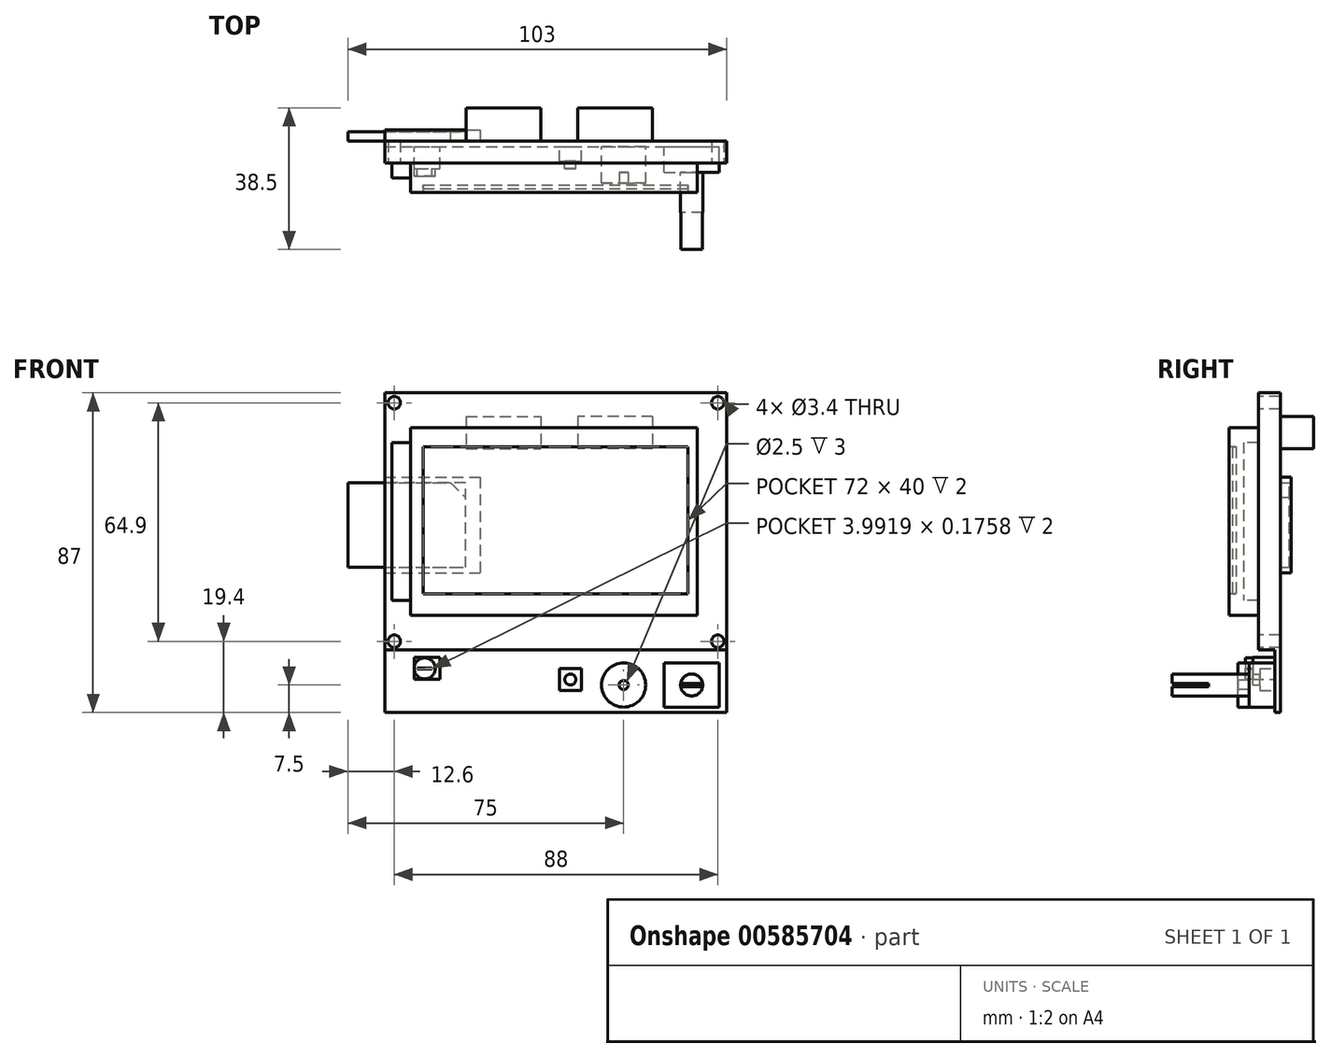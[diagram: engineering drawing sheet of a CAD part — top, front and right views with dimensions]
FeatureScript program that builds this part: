
annotation { "Feature Type Name" : "Feature", "Feature Type Description" : "" }
export const myFeature = defineFeature(function(context is Context, id is Id, definition is map)
    precondition{}
    {
        {
            var Q0;
            Q0=qCreatedBy(makeId("Front.planeOp"),FACE);
            var sketch = newSketch(context, id + "F0", { "sketchPlane" : qUnion([Q0])});
            skLineSegment(sketch, "E0.bottom", {"start": v(0, 0) * mm, "end": v(93, 0) * mm});
            skLineSegment(sketch, "E0.top", {"start": v(0, -87) * mm, "end": v(93, -87) * mm});
            skLineSegment(sketch, "E0.left", {"start": v(0, 0) * mm, "end": v(0, -87) * mm});
            skLineSegment(sketch, "E0.right", {"start": v(93, 0) * mm, "end": v(93, -87) * mm});
            skSolve(sketch);
        }
        {
            var Q0;
            Q0 = qSketchRegion(id + "F0", true);
            extrude(context, id + "F1", {"entities" : qUnion([Q0]), "oppositeDirection" : true, "depth" : 6 * mm, "offsetDistance" : 25 * mm});
        }
        {
            var Q0;
            Q0=makeQuery(id+"F1.opExtrude","CAP_FACE",FACE,{"disambiguationData":[OSD([sQuery(id+"F0.wireOp",EDGE,"E0.bottom"),sQuery(id+"F0.wireOp",EDGE,"E0.top"),sQuery(id+"F0.wireOp",EDGE,"E0.left"),sQuery(id+"F0.wireOp",EDGE,"E0.right")])],"isStart":true});
            var sketch = newSketch(context, id + "F2", { "sketchPlane" : qUnion([Q0])});
            skLineSegment(sketch, "E1.bottom", {"start": v(7, -9.5) * mm, "end": v(85, -9.5) * mm});
            skLineSegment(sketch, "E1.top", {"start": v(7, -60.5) * mm, "end": v(85, -60.5) * mm});
            skLineSegment(sketch, "E1.left", {"start": v(7, -9.5) * mm, "end": v(7, -60.5) * mm});
            skLineSegment(sketch, "E1.right", {"start": v(85, -9.5) * mm, "end": v(85, -60.5) * mm});
            skSolve(sketch);
        }
        {
            var Q0;
            Q0 = qSketchRegion(id + "F2", true);
            extrude(context, id + "F3", {"entities" : qUnion([Q0]), "operationType" : NewBodyOperationType.ADD, "depth" : 8 * mm, "offsetDistance" : 25 * mm});
        }
        {
            var Q0;
            Q0=makeQuery(id+"F3.opExtrude","CAP_FACE",FACE,{"disambiguationData":[OSD([sQuery(id+"F2.wireOp",EDGE,"E1.bottom"),sQuery(id+"F2.wireOp",EDGE,"E1.top"),sQuery(id+"F2.wireOp",EDGE,"E1.left"),sQuery(id+"F2.wireOp",EDGE,"E1.right")])],"isStart":false});
            var sketch = newSketch(context, id + "F4", { "sketchPlane" : qUnion([Q0])});
            skLineSegment(sketch, "E2.bottom", {"start": v(10.5, -14.75) * mm, "end": v(82.5, -14.75) * mm});
            skLineSegment(sketch, "E2.top", {"start": v(10.5, -54.75) * mm, "end": v(82.5, -54.75) * mm});
            skLineSegment(sketch, "E2.left", {"start": v(10.5, -14.75) * mm, "end": v(10.5, -54.75) * mm});
            skLineSegment(sketch, "E2.right", {"start": v(82.5, -14.75) * mm, "end": v(82.5, -54.75) * mm});
            skSolve(sketch);
        }
        {
            var Q0;
            Q0 = qSketchRegion(id + "F4", true);
            extrude(context, id + "F5", {"entities" : qUnion([Q0]), "operationType" : NewBodyOperationType.REMOVE, "oppositeDirection" : true, "depth" : 2 * mm, "offsetDistance" : 25 * mm});
        }
        {
            var Q0;
            Q0=makeQuery(id+"F1.opExtrude","CAP_FACE",FACE,{"disambiguationData":[OSD([sQuery(id+"F0.wireOp",EDGE,"E0.bottom"),sQuery(id+"F0.wireOp",EDGE,"E0.top"),sQuery(id+"F0.wireOp",EDGE,"E0.left"),sQuery(id+"F0.wireOp",EDGE,"E0.right")])],"isStart":true});
            var sketch = newSketch(context, id + "F6", { "sketchPlane" : qUnion([Q0])});
            skCircle(sketch, "E3", {"center": v(2.6, -2.7) * mm, "radius": 1.7 * mm});
            skCircle(sketch, "E4.MirrorC", {"center": v(90.6, -2.7) * mm, "radius": 1.7 * mm});
            skLineSegment(sketch, "E5", {"start": v(0, -70) * mm, "end": v(93, -70) * mm, "construction": true});
            skCircle(sketch, "E6.MirrorC", {"center": v(90.6, -67.6) * mm, "radius": 1.7 * mm});
            skCircle(sketch, "E7.MirrorC", {"center": v(2.6, -67.6) * mm, "radius": 1.7 * mm});
            skPoint(sketch, "E8.0", {"position": v(93, 0) * mm});
            skLineSegment(sketch, "E9.0", {"start": v(0, 0) * mm, "end": v(93, 0) * mm, "construction": true});
            skLineSegment(sketch, "E10.0", {"start": v(93, 0) * mm, "end": v(93, -87) * mm, "construction": true});
            skSolve(sketch);
        }
        {
            var Q0;
            Q0 = qSketchRegion(id + "F6", true);
            extrude(context, id + "F7", {"entities" : qUnion([Q0]), "operationType" : NewBodyOperationType.REMOVE, "oppositeDirection" : true, "depth" : 25 * mm, "offsetDistance" : 25 * mm});
        }
        {
            var Q0;
            Q0=makeQuery(id+"F3.opExtrude","SWEPT_FACE",FACE,{"disambiguationData":[OSD([sQuery(id+"F2.wireOp",EDGE,"E1.left")])]});
            var sketch = newSketch(context, id + "F8", { "sketchPlane" : qUnion([Q0])});
            skLineSegment(sketch, "E11.bottom", {"start": v(0, -13.5) * mm, "end": v(4, -13.5) * mm});
            skLineSegment(sketch, "E11.top", {"start": v(0, -56.5) * mm, "end": v(4, -56.5) * mm});
            skLineSegment(sketch, "E11.left", {"start": v(0, -13.5) * mm, "end": v(0, -56.5) * mm});
            skLineSegment(sketch, "E11.right", {"start": v(4, -13.5) * mm, "end": v(4, -56.5) * mm});
            skSolve(sketch);
        }
        {
            var Q0;
            Q0 = qSketchRegion(id + "F8", true);
            extrude(context, id + "F9", {"entities" : qUnion([Q0]), "operationType" : NewBodyOperationType.ADD, "depth" : 5 * mm, "offsetDistance" : 25 * mm});
        }
        {
            var Q0;
            Q0=makeQuery(id+"F6.imprint","IMPRINT",FACE,{"disambiguationData":[TD([[makeQuery(id+"F6.imprint","IMPRINT",EDGE,{"derivedFrom":sQuery(id+"F6.wireOp",EDGE,"E3")}),-1.0]])]});
            var sketch = newSketch(context, id + "F10", { "sketchPlane" : qUnion([Q0])});
            skLineSegment(sketch, "E12.0", {"start": v(0, -70) * mm, "end": v(93, -70) * mm});
            skLineSegment(sketch, "E13.0", {"start": v(0, -70) * mm, "end": v(0, -87) * mm});
            skLineSegment(sketch, "E14.0", {"start": v(0, -87) * mm, "end": v(93, -87) * mm});
            skLineSegment(sketch, "E15.0", {"start": v(93, -70) * mm, "end": v(93, -87) * mm});
            skPoint(sketch, "E16.orphan", {"position": v(0, 0) * mm});
            skPoint(sketch, "E17.orphan", {"position": v(93, 0) * mm});
            skSolve(sketch);
        }
        {
            var Q0;
            Q0 = qSketchRegion(id + "F10", true);
            extrude(context, id + "F11", {"entities" : qUnion([Q0]), "operationType" : NewBodyOperationType.REMOVE, "oppositeDirection" : true, "depth" : 4.5 * mm, "offsetDistance" : 25 * mm});
        }
        {
            var Q0;
            Q0=makeQuery(id+"F11.boolean.opBoolean","COPY",FACE,{"derivedFrom":makeQuery(id+"F11.opExtrude","CAP_FACE",FACE,{"disambiguationData":[OSD([sQuery(id+"F10.wireOp",EDGE,"E12.0"),sQuery(id+"F10.wireOp",EDGE,"E13.0"),sQuery(id+"F10.wireOp",EDGE,"E14.0"),sQuery(id+"F10.wireOp",EDGE,"E15.0")])],"isStart":false})});
            var sketch = newSketch(context, id + "F12", { "sketchPlane" : qUnion([Q0])});
            skLineSegment(sketch, "E18.bottom", {"start": v(76, -73.5) * mm, "end": v(91, -73.5) * mm});
            skLineSegment(sketch, "E18.top", {"start": v(76, -85.5) * mm, "end": v(91, -85.5) * mm});
            skLineSegment(sketch, "E18.left", {"start": v(76, -73.5) * mm, "end": v(76, -85.5) * mm});
            skLineSegment(sketch, "E18.right", {"start": v(91, -73.5) * mm, "end": v(91, -85.5) * mm});
            skLineSegment(sketch, "E19.bottom", {"start": v(47.5, -75) * mm, "end": v(53.5, -75) * mm});
            skLineSegment(sketch, "E19.top", {"start": v(47.5, -81) * mm, "end": v(53.5, -81) * mm});
            skLineSegment(sketch, "E19.left", {"start": v(47.5, -75) * mm, "end": v(47.5, -81) * mm});
            skLineSegment(sketch, "E19.right", {"start": v(53.5, -75) * mm, "end": v(53.5, -81) * mm});
            skLineSegment(sketch, "E20.bottom", {"start": v(8, -72) * mm, "end": v(15, -72) * mm});
            skLineSegment(sketch, "E20.top", {"start": v(8, -78) * mm, "end": v(15, -78) * mm});
            skLineSegment(sketch, "E20.left", {"start": v(8, -72) * mm, "end": v(8, -78) * mm});
            skLineSegment(sketch, "E20.right", {"start": v(15, -72) * mm, "end": v(15, -78) * mm});
            skCircle(sketch, "E21", {"center": v(65, -79.5) * mm, "radius": 6 * mm});
            skLineSegment(sketch, "E22", {"start": v(53.5, -78) * mm, "end": v(47.5, -78) * mm, "construction": true});
            skSolve(sketch);
        }
        {
            var Q0;
            Q0 = qSketchRegion(id + "F12", true);
            extrude(context, id + "F13", {"entities" : qUnion([Q0]), "operationType" : NewBodyOperationType.ADD, "depth" : 4 * mm, "offsetDistance" : 25 * mm});
        }
        {
            var Q0;
            Q0=makeQuery(id+"F13.opExtrude","CAP_FACE",FACE,{"disambiguationData":[OSD([sQuery(id+"F12.wireOp",EDGE,"E18.bottom"),sQuery(id+"F12.wireOp",EDGE,"E18.top"),sQuery(id+"F12.wireOp",EDGE,"E18.left"),sQuery(id+"F12.wireOp",EDGE,"E18.right")])],"isStart":false});
            extrude(context, id + "F14", {"entities" : qUnion([Q0]), "operationType" : NewBodyOperationType.ADD, "depth" : 3 * mm, "offsetDistance" : 25 * mm});
        }
        {
            var Q0;
            Q0=makeQuery(id+"F13.opExtrude","CAP_FACE",FACE,{"disambiguationData":[OSD([sQuery(id+"F12.wireOp",EDGE,"E20.bottom"),sQuery(id+"F12.wireOp",EDGE,"E20.top"),sQuery(id+"F12.wireOp",EDGE,"E20.left"),sQuery(id+"F12.wireOp",EDGE,"E20.right")])],"isStart":false});
            extrude(context, id + "F15", {"entities" : qUnion([Q0]), "operationType" : NewBodyOperationType.ADD, "depth" : 2 * mm, "offsetDistance" : 25 * mm});
        }
        {
            var Q0;
            Q0=makeQuery(id+"F13.opExtrude","CAP_FACE",FACE,{"disambiguationData":[OSD([sQuery(id+"F12.wireOp",EDGE,"E21")])],"isStart":false});
            extrude(context, id + "F16", {"entities" : qUnion([Q0]), "operationType" : NewBodyOperationType.ADD, "depth" : 6 * mm, "offsetDistance" : 25 * mm});
        }
        {
            var Q0;
            Q0=makeQuery(id+"F15.opExtrude","CAP_FACE",FACE,{"disambiguationData":[OSD([sQuery(id+"F12.wireOp",EDGE,"E20.bottom"),sQuery(id+"F12.wireOp",EDGE,"E20.top"),sQuery(id+"F12.wireOp",EDGE,"E20.left"),sQuery(id+"F12.wireOp",EDGE,"E20.right")])],"isStart":false});
            var sketch = newSketch(context, id + "F17", { "sketchPlane" : qUnion([Q0])});
            skCircle(sketch, "E23", {"center": v(10.88, -75) * mm, "radius": 2.88 * mm});
            skPoint(sketch, "E23.centerSnap0", {"position": v(8, -75) * mm});
            skLineSegment(sketch, "E24.bottom", {"start": v(8.83, -74.91) * mm, "end": v(12.82, -74.91) * mm});
            skLineSegment(sketch, "E24.top", {"start": v(8.83, -75) * mm, "end": v(12.82, -75) * mm, "construction": true});
            skLineSegment(sketch, "E24.left", {"start": v(8.83, -74.91) * mm, "end": v(8.83, -75) * mm});
            skLineSegment(sketch, "E24.right", {"start": v(12.82, -74.91) * mm, "end": v(12.82, -75) * mm});
            skLineSegment(sketch, "E25.MirrorCS", {"start": v(8.83, -75.09) * mm, "end": v(12.82, -75.09) * mm});
            skLineSegment(sketch, "E26.MirrorCS", {"start": v(12.82, -75.09) * mm, "end": v(12.82, -75) * mm});
            skLineSegment(sketch, "E27.MirrorCS", {"start": v(8.83, -75.09) * mm, "end": v(8.83, -75) * mm});
            skSolve(sketch);
        }
        {
            var Q0;
            Q0=makeQuery(id+"F17.imprint","IMPRINT",FACE,{"disambiguationData":[TD([[makeQuery(id+"F17.imprint","IMPRINT",EDGE,{"derivedFrom":sQuery(id+"F17.wireOp",EDGE,"E23")}),1.0]])]});
            extrude(context, id + "F18", {"entities" : qUnion([Q0]), "operationType" : NewBodyOperationType.ADD, "depth" : 2 * mm, "offsetDistance" : 25 * mm});
        }
        {
            var Q0;
            Q0=makeQuery(id+"F13.opExtrude","CAP_FACE",FACE,{"disambiguationData":[OSD([sQuery(id+"F12.wireOp",EDGE,"E19.bottom"),sQuery(id+"F12.wireOp",EDGE,"E19.top"),sQuery(id+"F12.wireOp",EDGE,"E19.left"),sQuery(id+"F12.wireOp",EDGE,"E19.right")])],"isStart":false});
            var sketch = newSketch(context, id + "F19", { "sketchPlane" : qUnion([Q0])});
            skCircle(sketch, "E28", {"center": v(50.5, -78) * mm, "radius": 1.5 * mm});
            skPoint(sketch, "E28.centerSnap0", {"position": v(47.5, -78) * mm});
            skPoint(sketch, "E28.centerSnap1", {"position": v(50.5, -75) * mm});
            skSolve(sketch);
        }
        {
            var Q0;
            Q0 = qSketchRegion(id + "F19", true);
            extrude(context, id + "F20", {"entities" : qUnion([Q0]), "operationType" : NewBodyOperationType.ADD, "depth" : 2 * mm, "offsetDistance" : 25 * mm});
        }
        {
            var Q0;
            Q0=makeQuery(id+"F16.opExtrude","CAP_FACE",FACE,{"disambiguationData":[OSD([sQuery(id+"F12.wireOp",EDGE,"E21")])],"isStart":false});
            var sketch = newSketch(context, id + "F21", { "sketchPlane" : qUnion([Q0])});
            skCircle(sketch, "E29", {"center": v(65, -79.5) * mm, "radius": 1.25 * mm});
            skSolve(sketch);
        }
        {
            var Q0;
            Q0 = qSketchRegion(id + "F21", true);
            extrude(context, id + "F22", {"entities" : qUnion([Q0]), "operationType" : NewBodyOperationType.REMOVE, "oppositeDirection" : true, "depth" : 3 * mm, "offsetDistance" : 25 * mm});
        }
        {
            var Q0;
            Q0=makeQuery(id+"F14.opExtrude","CAP_FACE",FACE,{"disambiguationData":[OSD([sQuery(id+"F12.wireOp",EDGE,"E18.bottom"),sQuery(id+"F12.wireOp",EDGE,"E18.top"),sQuery(id+"F12.wireOp",EDGE,"E18.left"),sQuery(id+"F12.wireOp",EDGE,"E18.right")])],"isStart":false});
            var sketch = newSketch(context, id + "F23", { "sketchPlane" : qUnion([Q0])});
            skCircle(sketch, "E30", {"center": v(83.5, -79.5) * mm, "radius": 3 * mm});
            skPoint(sketch, "E30.centerSnap0", {"position": v(83.5, -73.5) * mm});
            skPoint(sketch, "E30.centerSnap1", {"position": v(76, -79.5) * mm});
            skSolve(sketch);
        }
        {
            var Q0;
            Q0 = qSketchRegion(id + "F23", true);
            extrude(context, id + "F24", {"entities" : qUnion([Q0]), "operationType" : NewBodyOperationType.ADD, "depth" : 21 * mm, "offsetDistance" : 25 * mm});
        }
        {
            var Q0;
            Q0=makeQuery(id+"F24.opExtrude","CAP_FACE",FACE,{"disambiguationData":[OSD([sQuery(id+"F23.wireOp",EDGE,"E30")])],"isStart":false});
            var sketch = newSketch(context, id + "F25", { "sketchPlane" : qUnion([Q0])});
            skLineSegment(sketch, "E31.bottom", {"start": v(86.9, -79.95) * mm, "end": v(80.1, -79.95) * mm});
            skLineSegment(sketch, "E31.top", {"start": v(86.9, -79.05) * mm, "end": v(80.1, -79.05) * mm});
            skLineSegment(sketch, "E31.left", {"start": v(86.9, -79.95) * mm, "end": v(86.9, -79.05) * mm});
            skLineSegment(sketch, "E31.right", {"start": v(80.1, -79.95) * mm, "end": v(80.1, -79.05) * mm});
            skPoint(sketch, "E31.middle", {"position": v(83.5, -79.5) * mm});
            skSolve(sketch);
        }
        {
            var Q0;
            Q0 = qSketchRegion(id + "F25", true);
            extrude(context, id + "F26", {"entities" : qUnion([Q0]), "operationType" : NewBodyOperationType.REMOVE, "oppositeDirection" : true, "depth" : 10 * mm, "offsetDistance" : 25 * mm});
        }
        {
            var Q0;
            Q0=makeQuery(id+"F1.opExtrude","CAP_FACE",FACE,{"disambiguationData":[OSD([sQuery(id+"F0.wireOp",EDGE,"E0.bottom"),sQuery(id+"F0.wireOp",EDGE,"E0.top"),sQuery(id+"F0.wireOp",EDGE,"E0.left"),sQuery(id+"F0.wireOp",EDGE,"E0.right")])],"isStart":false});
            var sketch = newSketch(context, id + "F27", { "sketchPlane" : qUnion([Q0])});
            skLineSegment(sketch, "E32.bottom", {"start": v(0, -23) * mm, "end": v(-26, -23) * mm});
            skLineSegment(sketch, "E32.top", {"start": v(0, -49) * mm, "end": v(-26, -49) * mm});
            skLineSegment(sketch, "E32.left", {"start": v(0, -23) * mm, "end": v(0, -49) * mm});
            skLineSegment(sketch, "E32.right", {"start": v(-26, -23) * mm, "end": v(-26, -49) * mm});
            skSolve(sketch);
        }
        {
            var Q0;
            Q0 = qSketchRegion(id + "F27", true);
            extrude(context, id + "F28", {"entities" : qUnion([Q0]), "operationType" : NewBodyOperationType.ADD, "depth" : 3 * mm, "offsetDistance" : 25 * mm});
        }
        {
            var Q0;
            Q0=makeQuery(id+"F28.boolean.opBoolean","MERGE",FACE,{"derivedFrom":[makeQuery(id+"F1.opExtrude","SWEPT_FACE",FACE,{"disambiguationData":[OSD([sQuery(id+"F0.wireOp",EDGE,"E0.left")])]}),makeQuery(id+"F28.opExtrude","SWEPT_FACE",FACE,{"disambiguationData":[OSD([sQuery(id+"F27.wireOp",EDGE,"E32.left")])]})]});
            var sketch = newSketch(context, id + "F29", { "sketchPlane" : qUnion([Q0])});
            skLineSegment(sketch, "E33.bottom", {"start": v(-6, -47.5) * mm, "end": v(-8.5, -47.5) * mm});
            skLineSegment(sketch, "E33.top", {"start": v(-6, -24.5) * mm, "end": v(-8.5, -24.5) * mm});
            skLineSegment(sketch, "E33.left", {"start": v(-6, -47.5) * mm, "end": v(-6, -24.5) * mm});
            skLineSegment(sketch, "E33.right", {"start": v(-8.5, -47.5) * mm, "end": v(-8.5, -24.5) * mm});
            skSolve(sketch);
        }
        {
            var Q0;
            Q0 = qSketchRegion(id + "F29", true);
            extrude(context, id + "F30", {"entities" : qUnion([Q0]), "operationType" : NewBodyOperationType.REMOVE, "oppositeDirection" : true, "depth" : 22 * mm, "offsetDistance" : 25 * mm});
        }
        {
            var Q0;
            Q0=makeQuery(id+"F30.boolean.opBoolean","COPY",FACE,{"derivedFrom":makeQuery(id+"F30.opExtrude","CAP_FACE",FACE,{"disambiguationData":[OSD([sQuery(id+"F29.wireOp",EDGE,"E33.bottom"),sQuery(id+"F29.wireOp",EDGE,"E33.top"),sQuery(id+"F29.wireOp",EDGE,"E33.left"),sQuery(id+"F29.wireOp",EDGE,"E33.right")])],"isStart":false})});
            extrude(context, id + "F31", {"entities" : qUnion([Q0]), "depth" : 32 * mm, "offsetDistance" : 25 * mm});
        }
        {
            var Q0;
            Q0=makeQuery(id+"F31.opExtrude","CAP_EDGE",EDGE,{"disambiguationData":[OSD([sQuery(id+"F29.wireOp",EDGE,"E33.top")])],"isStart":true});
            chamfer(context, id + "F32", {"entities" : qUnion([Q0]), "width" : 4 * mm, "tangentPropagation" : true});
        }
        {
            var Q0;
            Q0=makeQuery(id+"F1.opExtrude","CAP_FACE",FACE,{"disambiguationData":[OSD([sQuery(id+"F0.wireOp",EDGE,"E0.bottom"),sQuery(id+"F0.wireOp",EDGE,"E0.top"),sQuery(id+"F0.wireOp",EDGE,"E0.left"),sQuery(id+"F0.wireOp",EDGE,"E0.right")])],"isStart":false});
            var sketch = newSketch(context, id + "F33", { "sketchPlane" : qUnion([Q0])});
            skLineSegment(sketch, "E34.bottom", {"start": v(-72.85, -6.5) * mm, "end": v(-52.5, -6.5) * mm});
            skLineSegment(sketch, "E34.top", {"start": v(-72.85, -15.2) * mm, "end": v(-52.5, -15.2) * mm});
            skLineSegment(sketch, "E34.left", {"start": v(-72.85, -6.5) * mm, "end": v(-72.85, -15.2) * mm});
            skLineSegment(sketch, "E34.right", {"start": v(-52.5, -6.5) * mm, "end": v(-52.5, -15.2) * mm});
            skLineSegment(sketch, "E35", {"start": v(-47.5, -3.08) * mm, "end": v(-47.5, -33.11) * mm, "construction": true});
            skLineSegment(sketch, "E36.MirrorCS", {"start": v(-22.15, -15.2) * mm, "end": v(-42.5, -15.2) * mm});
            skLineSegment(sketch, "E37.MirrorCS", {"start": v(-22.15, -6.5) * mm, "end": v(-42.5, -6.5) * mm});
            skLineSegment(sketch, "E38.MirrorCS", {"start": v(-22.15, -6.5) * mm, "end": v(-22.15, -15.2) * mm});
            skLineSegment(sketch, "E39.MirrorCS", {"start": v(-42.5, -6.5) * mm, "end": v(-42.5, -15.2) * mm});
            skSolve(sketch);
        }
        {
            var Q0;
            Q0=makeQuery(id+"F33.imprint","IMPRINT",FACE,{"disambiguationData":[TD([[makeQuery(id+"F33.imprint","IMPRINT",EDGE,{"derivedFrom":sQuery(id+"F33.wireOp",EDGE,"E34.bottom")}),-1.0]])]});
            var Q1;
            Q1=makeQuery(id+"F33.imprint","IMPRINT",FACE,{"disambiguationData":[TD([[makeQuery(id+"F33.imprint","IMPRINT",EDGE,{"derivedFrom":sQuery(id+"F33.wireOp",EDGE,"E36.MirrorCS")}),-1.0]])]});
            extrude(context, id + "F34", {"entities" : qUnion([Q0, Q1]), "operationType" : NewBodyOperationType.ADD, "depth" : 9 * mm, "offsetDistance" : 25 * mm});
        }
        {
            var Q0;
            Q0=makeQuery(id+"F5.boolean.opBoolean","COPY",FACE,{"derivedFrom":makeQuery(id+"F5.opExtrude","CAP_FACE",FACE,{"disambiguationData":[OSD([sQuery(id+"F4.wireOp",EDGE,"E2.bottom"),sQuery(id+"F4.wireOp",EDGE,"E2.top"),sQuery(id+"F4.wireOp",EDGE,"E2.left"),sQuery(id+"F4.wireOp",EDGE,"E2.right")])],"isStart":false})});
            extrude(context, id + "F35", {"entities" : qUnion([Q0]), "depth" : 1 * mm, "offsetDistance" : 25 * mm});
        }
    });
